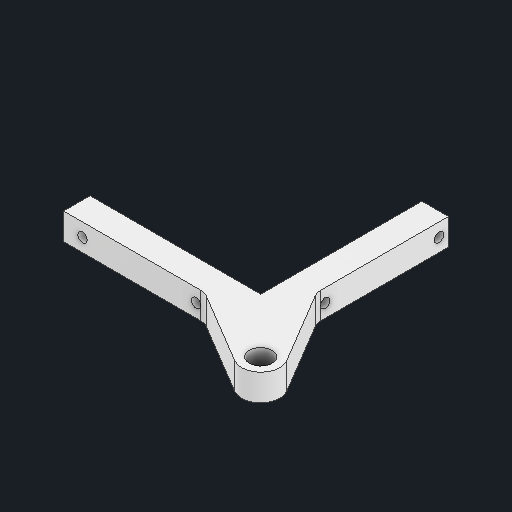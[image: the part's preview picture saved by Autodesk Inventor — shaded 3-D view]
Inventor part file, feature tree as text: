
AUTODESK INVENTOR PART (.ipt)
format: ipt  version: 2022 (Build 260153000, 153)  size: 139,264 bytes
history: native  units: mm
features: extrude x3, sketch x3
ambient origin geometry x8: Origin, YZ Plane, XZ Plane, XY Plane, X Axis, Y Axis, Z Axis, Center Point
bodies: Solid1 (feature_tree)
feature tree (6):
  extrude  "Extrusion1"  Depth=25.0mm
  extrude  "Extrusion2"  Depth=7.0mm
  extrude  "Extrusion3"  TaperAngle=135.0deg  [1 undecoded]
  sketch  "Sketch1"  dims[d0=35.0mm d2=25.0mm]
  sketch  "Sketch2"  dims[d3=45.0mm d4=7.0mm]
  sketch  "Sketch3"  dims[d5=7.0mm d6=135.0deg d7=6.0mm d8=10.0mm d9=4.0mm d10=7.0mm d11=0.0mm d12=10.0mm d13=30.0mm d14=2.5mm d15=2.5mm d16=7.0mm d17=0.0mm d18=10.0mm d19=30.0mm d20=2.5mm d21=2.5mm d22=10.0mm d23=0.0mm]
note: 1 required parameter value undecoded (feature->parameter linkage not recoverable at this tier; creation-order binding heuristic only, values carry confidence <= 0.55)
